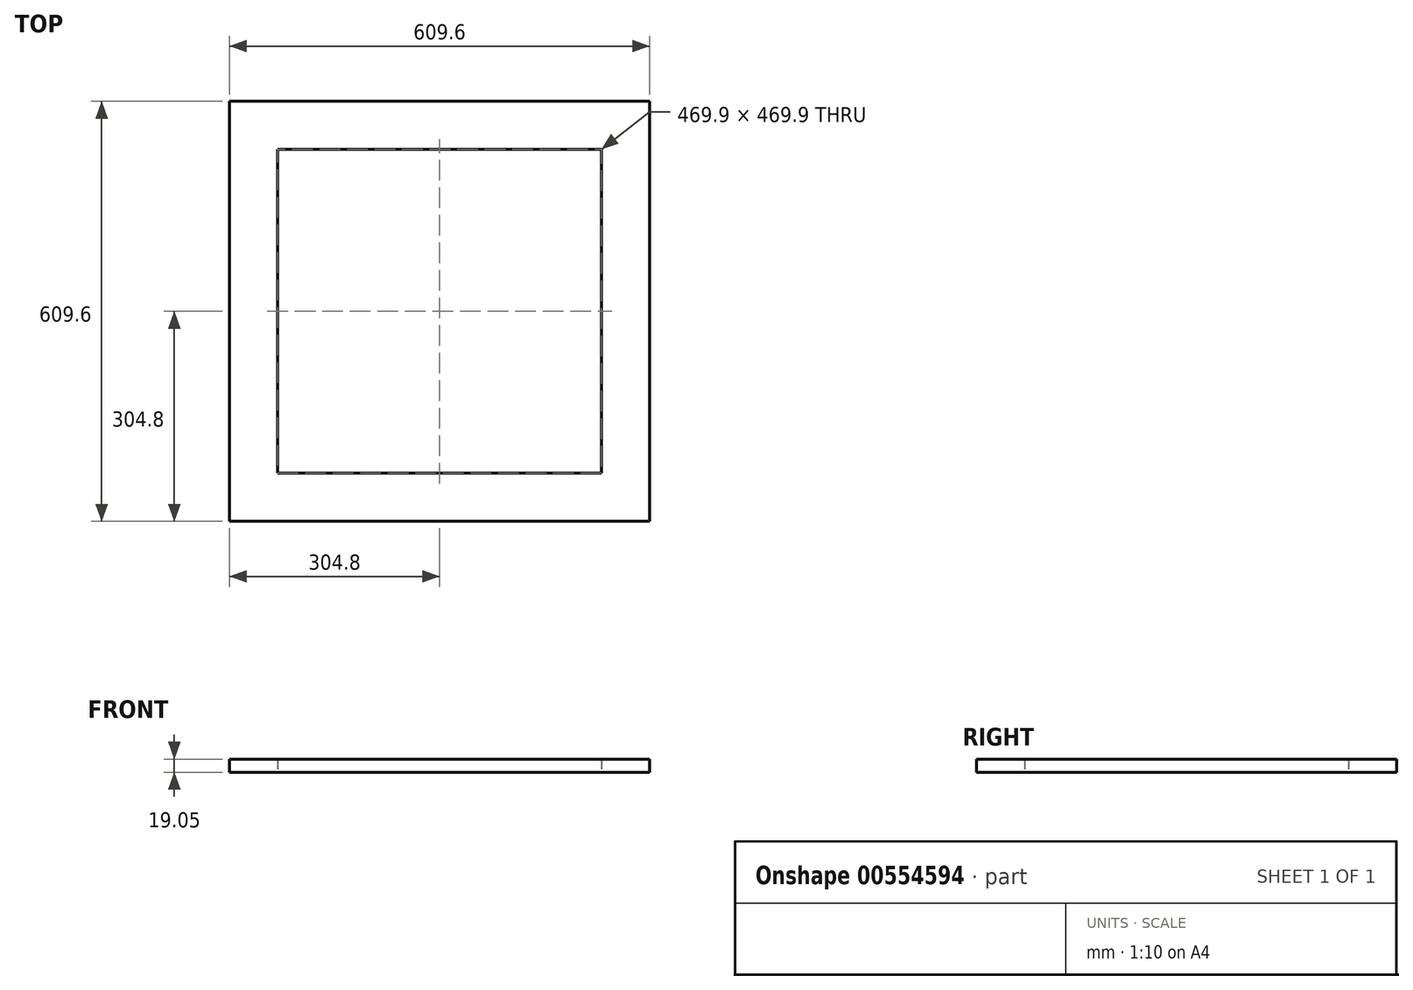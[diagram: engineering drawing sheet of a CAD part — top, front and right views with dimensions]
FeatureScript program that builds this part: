
annotation { "Feature Type Name" : "Feature", "Feature Type Description" : "" }
export const myFeature = defineFeature(function(context is Context, id is Id, definition is map)
    precondition{}
    {
        {
            var Q0;
            Q0=qCreatedBy(makeId("Top.planeOp"),FACE);
            var sketch = newSketch(context, id + "F0", { "sketchPlane" : qUnion([Q0])});
            skLineSegment(sketch, "E0.bottom", {"start": v(304.8, 304.8) * mm, "end": v(-304.8, 304.8) * mm});
            skLineSegment(sketch, "E0.top", {"start": v(304.8, -304.8) * mm, "end": v(-304.8, -304.8) * mm});
            skLineSegment(sketch, "E0.left", {"start": v(304.8, 304.8) * mm, "end": v(304.8, -304.8) * mm});
            skLineSegment(sketch, "E0.right", {"start": v(-304.8, 304.8) * mm, "end": v(-304.8, -304.8) * mm});
            skPoint(sketch, "E0.middle", {"position": v(0, 0) * mm});
            skLineSegment(sketch, "E1.bottom", {"start": v(234.95, 234.95) * mm, "end": v(-234.95, 234.95) * mm});
            skLineSegment(sketch, "E1.top", {"start": v(234.95, -234.95) * mm, "end": v(-234.95, -234.95) * mm});
            skLineSegment(sketch, "E1.left", {"start": v(234.95, 234.95) * mm, "end": v(234.95, -234.95) * mm});
            skLineSegment(sketch, "E1.right", {"start": v(-234.95, 234.95) * mm, "end": v(-234.95, -234.95) * mm});
            skSolve(sketch);
        }
        {
            var Q0;
            Q0=makeQuery(id+"F0.imprint","IMPRINT",FACE,{"disambiguationData":[TD([[makeQuery(id+"F0.imprint","IMPRINT",EDGE,{"derivedFrom":sQuery(id+"F0.wireOp",EDGE,"E0.bottom")}),1.0]])]});
            extrude(context, id + "F1", {"entities" : qUnion([Q0]), "depth" : 19.05 * mm, "offsetDistance" : 25.4 * mm});
        }
    });
